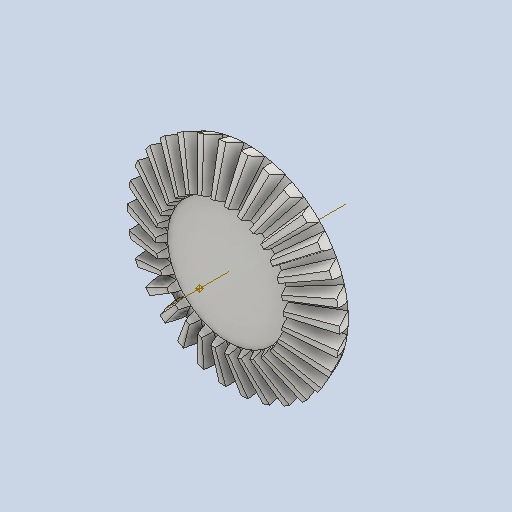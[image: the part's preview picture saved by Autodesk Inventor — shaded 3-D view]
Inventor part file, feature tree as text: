
AUTODESK INVENTOR PART (.ipt)
format: ipt  version: 2022 (Build 260153000, 153)  size: 629,248 bytes
history: native  units: mm
features: other x24, loft x2, pattern_circular x2, sketch x1
ambient origin geometry x6: Origin, XZ Plane, X Axis, Y Axis, Z Axis, Center Point
bodies: Solid1 (feature_tree)
feature tree (29):
  other  "Top Point"
  other  "Mesh Plane2"
  other  "Teeth Body"
  other  "Start Point"
  other  "Tooth Plane"
  other  "Start Sketch"
  other  "End Point"
  other  "3D Sketch Right"
  other  "End Plane Right"
  loft  "Loft Right"
  pattern_circular  "Circular Pattern Right"  [2 undecoded]
  other  "3D Sketch Left"
  other  "End Plane Left"
  loft  "Loft Left"
  pattern_circular  "Circular Pattern Left"  [2 undecoded]
  other  "Fix Body"
  other  "Mesh Plane"
  other  "Top Plane"
  other  "Teeth Body Sketch"
  other  "End Plane"
  other  "End Sketch"
  other  "Helical Curve Left"
  other  "End Sketch Left"
  other  "Body Sketch"
  sketch  "Sketch6"  dims[d0=60.0mm d1=58.217325mm d2=61.485563mm d3=12.9mm d4=10.143047mm d5=90.0deg d7=21.163271mm d8=21.961152mm d9=75.095331mm d11=13.12mm d12=12.569844mm d15=13.043742mm d16=44.602586mm d17=0.0mm d18=90.0deg d19=0.0mm d20=90.0deg d21=300.0mm d22=360.0deg d26=153.943419mm d27=4.872646mm d28=60.0mm d29=-11.902899mm d30=12.569844mm d31=13.043742mm d32=44.602586mm d35=0.0mm d37=0.0mm d39=0.0mm d40=90.0deg d41=300.0mm d42=360.0deg d46=90.0deg d47=90.0deg d48=0.0mm d49=0.0mm d50=90.0deg d51=1.047198mm d52=0.0mm d53=0.0mm d54=0.0mm d56=6.915476mm d57=84.097472mm d58=77.849472mm d59=49.949373mm d60=46.238397mm d61=49.949373mm d62=46.238397mm d63=90.0deg d64=90.0deg d65=153.943419mm d66=31.5mm d67=60.0mm d68=-11.902899mm d69=4.872646mm d70=13.043742mm d71=44.602586mm d72=12.569844mm d73=46.238397mm d74=49.949373mm d75=0.0mm d76=90.0deg d77=0.0mm d78=90.0deg d79=0.0mm d80=90.0deg d81=300.0mm d82=360.0deg d84=10.0mm d85=20.0mm d86=20.0mm d87=10.0mm d88=0.0mm d89=0.0mm]
  other  "Srf1"
  other  "Helical Curve Right"
  other  "End Sketch Right"
  other  "Pitch Diameter"
note: 4 required parameter values undecoded (feature->parameter linkage not recoverable at this tier; creation-order binding heuristic only, values carry confidence <= 0.55)
